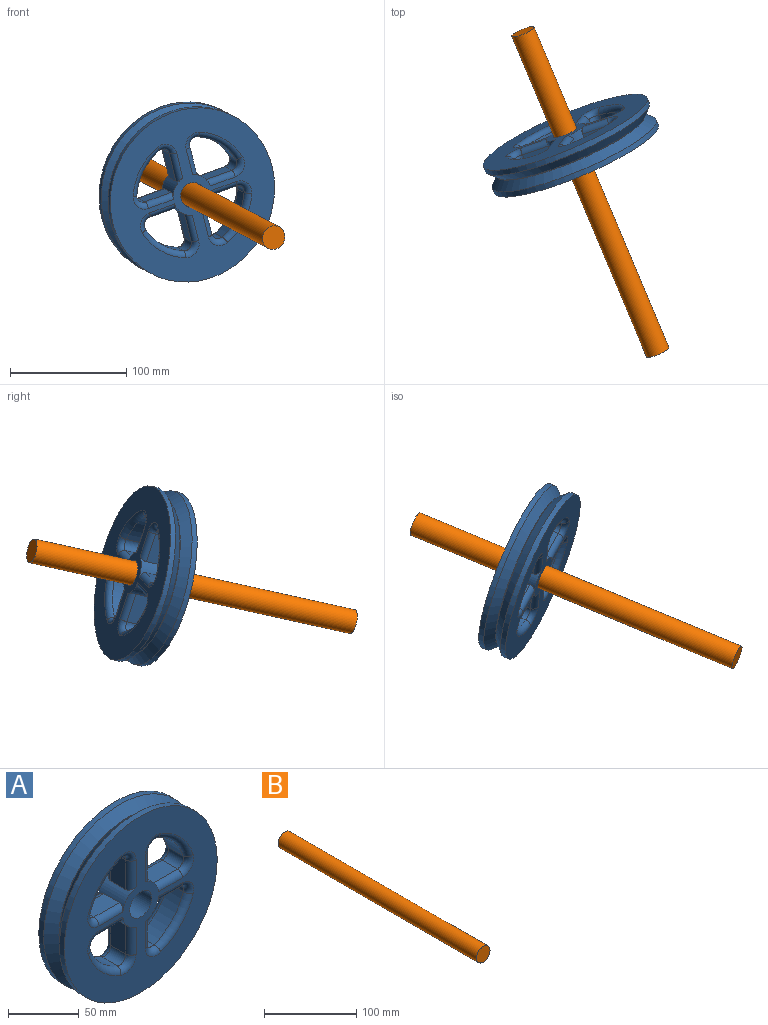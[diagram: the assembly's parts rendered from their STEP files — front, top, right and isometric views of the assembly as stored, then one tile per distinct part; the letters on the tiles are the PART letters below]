
ASSEMBLY  parts=2 mates=1
PART A: 85 faces, bbox 152.8x25.4x152.8 mm
  f0: cylinder r=76.39mm len=152.77mm, axis (0,1,0), area 2316.2mm2, adj f28,f84
  f1: cylinder r=6.35mm len=15.24mm, axis (0,1,0), area 188.4mm2, adj f2,f26,f47,f67
  f2: plane 25.66x15.24mm, normal (1,0,0), area 391mm2, adj f1,f3,f48,f68
  f3: cylinder r=17.92mm len=25.4mm, axis (0,1,0), area 291.1mm2, adj f2,f4,f27,f28,f44,f48,f64,f68
  f4: plane 25.21x15.24mm, normal (0,0,-1), area 384.2mm2, adj f3,f5,f44,f64
  f5: cylinder r=6.35mm len=15.24mm, axis (0,1,0), area 182.4mm2, adj f4,f26,f45,f65
  f6: cylinder r=6.35mm len=15.24mm, axis (0,1,0), area 182.4mm2, adj f7,f21,f32,f52
  f7: plane 25.21x15.24mm, normal (0,0,1), area 384.2mm2, adj f6,f8,f33,f53
  f8: cylinder r=17.92mm len=25.4mm, axis (0,1,0), area 291.1mm2, adj f7,f9,f27,f28,f29,f33,f49,f53
  f9: plane 25.66x15.24mm, normal (1,0,0), area 391mm2, adj f8,f10,f29,f49
  f10: cylinder r=6.35mm len=15.24mm, axis (0,1,0), area 188.4mm2, adj f9,f21,f30,f50
  f11: plane 25.66x15.24mm, normal (-1,0,0), area 391mm2, adj f12,f24,f34,f54
  f12: cylinder r=6.35mm len=15.24mm, axis (0,1,0), area 188.4mm2, adj f11,f13,f35,f55
  f13: cylinder r=50.12mm len=31.13mm, axis (0,1,0), area 672.9mm2, adj f12,f14,f36,f56
  f14: cylinder r=6.35mm len=15.24mm, axis (0,1,0), area 182.4mm2, adj f13,f15,f37,f57
  f15: plane 25.21x15.24mm, normal (0,0,-1), area 384.2mm2, adj f14,f24,f38,f58
  f16: plane 25.66x15.24mm, normal (-1,0,0), area 391mm2, adj f17,f25,f43,f63
  f17: cylinder r=17.92mm len=25.4mm, axis (0,1,0), area 291.1mm2, adj f16,f18,f27,f28,f39,f43,f59,f63
  f18: plane 25.21x15.24mm, normal (0,0,1), area 384.2mm2, adj f17,f19,f39,f59
  f19: cylinder r=6.35mm len=15.24mm, axis (0,1,0), area 182.4mm2, adj f18,f20,f40,f60
  f20: cylinder r=50.12mm len=31.13mm, axis (0,1,0), area 672.9mm2, adj f19,f25,f41,f61
  f21: cylinder r=50.12mm len=31.13mm, axis (0,1,0), area 672.9mm2, adj f6,f10,f31,f51
  f22: cylinder r=76.39mm len=152.77mm, axis (0,1,0), area 2316.2mm2, adj f27,f83
  f23: cylinder r=10.95mm len=25.4mm, axis (0,1,0), area 1748.3mm2, adj f27,f28
  f24: cylinder r=17.92mm len=25.4mm, axis (0,1,0), area 291.1mm2, adj f11,f15,f27,f28,f34,f38,f54,f58
  f25: cylinder r=6.35mm len=15.24mm, axis (0,1,0), area 188.4mm2, adj f16,f20,f42,f62
  f26: cylinder r=50.12mm len=31.13mm, axis (0,1,0), area 672.9mm2, adj f1,f5,f46,f66
  f27: plane 152.77x152.77mm, normal (0,-1,0), area 10783.7mm2, adj f3,f8,f17,f22,f23,f24,f29,f30
  f28: plane 152.77x152.77mm, normal (0,1,0), area 10783.7mm2, adj f0,f3,f8,f17,f23,f24,f49,f50
  f29: cylinder r=5.08mm len=25.66mm, axis (0,0,-1), area 197.2mm2, adj f8,f9,f27,f30
  f30: torus R=11.43mm, axis (0,-1,0), area 127.3mm2, adj f10,f27,f29,f31
  f31: torus R=55.2mm, axis (0,-1,0), area 365.3mm2, adj f21,f27,f30,f32
  f32: torus R=11.43mm, axis (0,-1,0), area 123.3mm2, adj f6,f27,f31,f33
  f33: cylinder r=5.08mm len=25.21mm, axis (1,0,0), area 196.3mm2, adj f7,f8,f27,f32
  f34: cylinder r=5.08mm len=25.66mm, axis (0,0,1), area 197.2mm2, adj f11,f24,f27,f35
  f35: torus R=11.43mm, axis (0,-1,0), area 127.3mm2, adj f12,f27,f34,f36
  f36: torus R=55.2mm, axis (0,-1,0), area 365.3mm2, adj f13,f27,f35,f37
  f37: torus R=11.43mm, axis (0,-1,0), area 123.3mm2, adj f14,f27,f36,f38
  f38: cylinder r=5.08mm len=25.21mm, axis (-1,0,0), area 196.3mm2, adj f15,f24,f27,f37
  f39: cylinder r=5.08mm len=25.21mm, axis (1,0,0), area 196.3mm2, adj f17,f18,f27,f40
  f40: torus R=11.43mm, axis (0,-1,0), area 123.3mm2, adj f19,f27,f39,f41
  f41: torus R=55.2mm, axis (0,-1,0), area 365.3mm2, adj f20,f27,f40,f42
  f42: torus R=11.43mm, axis (0,-1,0), area 127.3mm2, adj f25,f27,f41,f43
  f43: cylinder r=5.08mm len=25.66mm, axis (0,0,1), area 197.2mm2, adj f16,f17,f27,f42
  f44: cylinder r=5.08mm len=25.21mm, axis (-1,0,0), area 196.3mm2, adj f3,f4,f27,f45
  f45: torus R=11.43mm, axis (0,-1,0), area 123.3mm2, adj f5,f27,f44,f46
  f46: torus R=55.2mm, axis (0,-1,0), area 365.3mm2, adj f26,f27,f45,f47
  f47: torus R=11.43mm, axis (0,-1,0), area 127.3mm2, adj f1,f27,f46,f48
  f48: cylinder r=5.08mm len=25.66mm, axis (0,0,-1), area 197.2mm2, adj f2,f3,f27,f47
  f49: cylinder r=5.08mm len=25.66mm, axis (0,0,1), area 197.2mm2, adj f8,f9,f28,f50
  f50: torus R=11.43mm, axis (0,-1,0), area 127.3mm2, adj f10,f28,f49,f51
  f51: torus R=55.2mm, axis (0,-1,0), area 365.3mm2, adj f21,f28,f50,f52
  f52: torus R=11.43mm, axis (0,-1,0), area 123.3mm2, adj f6,f28,f51,f53
  f53: cylinder r=5.08mm len=25.21mm, axis (-1,0,0), area 196.3mm2, adj f7,f8,f28,f52
  f54: cylinder r=5.08mm len=25.66mm, axis (0,0,-1), area 197.2mm2, adj f11,f24,f28,f55
  f55: torus R=11.43mm, axis (0,-1,0), area 127.3mm2, adj f12,f28,f54,f56
  f56: torus R=55.2mm, axis (0,-1,0), area 365.3mm2, adj f13,f28,f55,f57
  f57: torus R=11.43mm, axis (0,-1,0), area 123.3mm2, adj f14,f28,f56,f58
  f58: cylinder r=5.08mm len=25.21mm, axis (1,0,0), area 196.3mm2, adj f15,f24,f28,f57
  f59: cylinder r=5.08mm len=25.21mm, axis (-1,0,0), area 196.3mm2, adj f17,f18,f28,f60
  f60: torus R=11.43mm, axis (0,-1,0), area 123.3mm2, adj f19,f28,f59,f61
  f61: torus R=55.2mm, axis (0,-1,0), area 365.3mm2, adj f20,f28,f60,f62
  f62: torus R=11.43mm, axis (0,-1,0), area 127.3mm2, adj f25,f28,f61,f63
  f63: cylinder r=5.08mm len=25.66mm, axis (0,0,-1), area 197.2mm2, adj f16,f17,f28,f62
  f64: cylinder r=5.08mm len=25.21mm, axis (1,0,0), area 196.3mm2, adj f3,f4,f28,f65
  f65: torus R=11.43mm, axis (0,-1,0), area 123.3mm2, adj f5,f28,f64,f66
  f66: torus R=55.2mm, axis (0,-1,0), area 365.3mm2, adj f26,f28,f65,f67
  f67: torus R=11.43mm, axis (0,-1,0), area 127.3mm2, adj f1,f28,f66,f68
  f68: cylinder r=5.08mm len=25.66mm, axis (0,0,1), area 197.2mm2, adj f2,f3,f28,f67
  f69: cylinder r=18.8mm len=22.95mm, axis (0,1,0), area 13.4mm2, adj f73,f80,f81,f82
  f70: cylinder r=18.8mm len=19.34mm, axis (0,1,0), area 10.7mm2, adj f71,f80,f81,f82
  f71: cylinder r=18.8mm len=19.34mm, axis (0,1,0), area 10.7mm2, adj f70,f78,f81,f82
  f72: cylinder r=18.8mm len=22.95mm, axis (0,1,0), area 13.4mm2, adj f78,f79,f81,f82
  f73: cylinder r=18.8mm len=22.95mm, axis (0,1,0), area 13.4mm2, adj f69,f74,f81,f82
  f74: cylinder r=62.57mm len=38.86mm, axis (0,1,0), area 28mm2, adj f73,f75,f81,f82
  f75: cylinder r=18.8mm len=19.34mm, axis (0,1,0), area 10.7mm2, adj f74,f76,f81,f82
  f76: cylinder r=18.8mm len=19.34mm, axis (0,1,0), area 10.7mm2, adj f75,f77,f81,f82
  f77: cylinder r=62.57mm len=38.86mm, axis (0,1,0), area 28mm2, adj f76,f79,f81,f82
  f78: cylinder r=62.57mm len=38.86mm, axis (0,1,0), area 28mm2, adj f71,f72,f81,f82
  f79: cylinder r=18.8mm len=22.95mm, axis (0,1,0), area 13.4mm2, adj f72,f77,f81,f82
  f80: cylinder r=62.57mm len=38.86mm, axis (0,1,0), area 28mm2, adj f69,f70,f81,f82
  f81: plane 137.53x137.53mm, normal (0,1,0), area 3079.1mm2, adj f69,f70,f71,f72,f73,f74,f75,f76
  f82: plane 137.53x137.53mm, normal (0,-1,0), area 3079.1mm2, adj f69,f70,f71,f72,f73,f74,f75,f76
  f83: cone r=76.39mm half-angle=45deg, axis (0,-1,0), area 4914.1mm2, adj f22,f81
  f84: cone r=68.77mm half-angle=45deg, axis (0,1,0), area 4914.1mm2, adj f0,f82
PART B: 3 faces, bbox 20.8x304.8x20.8 mm
  f0: cylinder r=10.39mm len=304.8mm, axis (0,1,0), area 19901.7mm2, adj f1,f2
  f1: plane 20.78x20.78mm, normal (0,-1,0), area 339.3mm2, adj f0
  f2: plane 20.78x20.78mm, normal (0,1,0), area 339.3mm2, adj f0
PLACE A rot(axis=(-0.97,-0.18,-0.15),165.1deg) t=(75.94,-4.9,26.99)mm
PLACE B rot(axis=(-0.96,-0.17,-0.25),163deg) t=(145.78,-170.91,-9.69)mm fixed
MATE cylindrical A.f23 <-> B.f0  axis (0.38,-0.9,-0.2) through (75.94,-4.9,26.99)mm
